# Revit family: Faucet_Touchless-Lavatory-KOHLER-STRAYT-K-72866T_1
name_source: partatom
category: Plumbing Fixtures
revit_build: Autodesk Revit 2017 (Build: 20160225_1515(x64)
units: mm (PartAtom-declared; Revit-internal decimal feet)

## family parameters
Cut with Voids When Loaded = No
Host = Face
OmniClass Number = 23.31.11.00
OmniClass Title = Faucets
Part Type = Normal
Room Calculation Point = No
Round Connector Dimension = Use Diameter
Shared = No

## types (1)
- CP-Polished Chrome
    ADA Compliant = No
    Apparent Load = 0 VA
    Assembly Code = D2010
    CW Connection = No
    Cold Water Inlet = Cold Water Inlet
    Date Modified = 6/18/2020
    Default Elevation = 36"
    Description = Slei Basin Induction Faucet-AC (single cooling type without AC power box)
    Drain Included = No
    Electrical Connector = Yes
    Electrical Note = DC 4 pieces of AA size alkaline batteries (LR06x4) AC 220V, frequency 50/60Hz
    Finish = Kohler-Metal-CP-Polished_Chrome
    Flow Rate = 1 GPM
    HW Connection = Yes
    Height = 5 7/16"
    Hot Water Inlet = Hot Water Inlet
    Length = 5 3/16"
    Manufacturer = KOHLER Co.
    Master Format 2014 = 22.41.39
    Master Format 2014 Name = Residential Faucets, Supplies, and Trim
    Material = Premium Metal Construction
    Model = K-72866T-CP
    Pressure = 0.00 psi
    Product Documentation Link = https://files.kohler.com.cn
    Product Name = STRAYT
    Product Page URL = https://www.kohler.com.cn
    Spout Reach = 5 3/16"
    Tempered Water Inlet = Tempered Water Inlet
    URL = http://www.kohler.com.cn
    Vent Connection = No
    Voltage = 220 V
    Waste Connection = No
    Waste Water Outlet = Waste Water Outlet
    WaterSense Certified = No
    Width = 2 1/16"

## geometry (parser evidence)
native form markers: Sweep x5
no freeform markers — native parametric forms only
